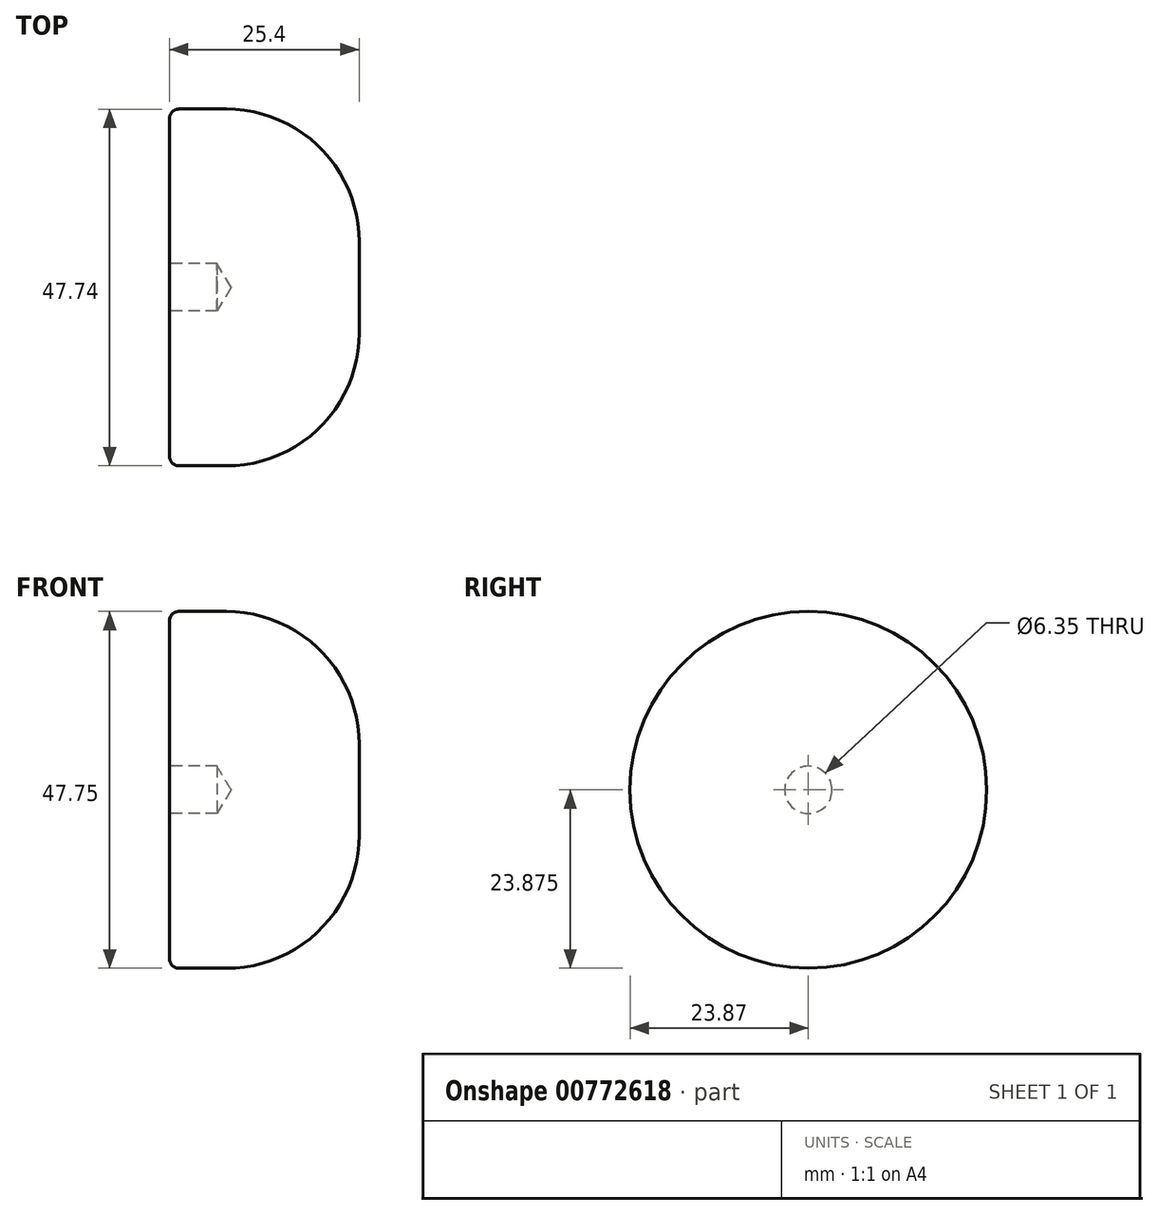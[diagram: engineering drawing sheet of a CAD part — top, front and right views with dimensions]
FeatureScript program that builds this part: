
annotation { "Feature Type Name" : "Feature", "Feature Type Description" : "" }
export const myFeature = defineFeature(function(context is Context, id is Id, definition is map)
    precondition{}
    {
        {
            var Q0;
            Q0=qCreatedBy(makeId("Right.planeOp"),FACE);
            var sketch = newSketch(context, id + "F0", { "sketchPlane" : qUnion([Q0])});
            skCircle(sketch, "E0", {"center": v(0, 17.6) * mm, "radius": 23.87 * mm});
            skSolve(sketch);
        }
        {
            var Q0;
            Q0 = qSketchRegion(id + "F0", true);
            extrude(context, id + "F1", {"entities" : qUnion([Q0]), "oppositeDirection" : true, "depth" : 25.4 * mm, "offsetDistance" : 25.4 * mm});
        }
        {
            var Q0;
            Q0=makeQuery(id+"F1.opExtrude","CAP_EDGE",EDGE,{"disambiguationData":[OSD([sQuery(id+"F0.wireOp",EDGE,"E0")])],"isStart":true});
            fillet(context, id + "F2", {"entities" : qUnion([Q0]), "radius" : 17.78 * mm, "tangentPropagation" : true, "allowEdgeOverflow" : false});
        }
        {
            var Q0;
            Q0=makeQuery(id+"F1.opExtrude","CAP_FACE",FACE,{"disambiguationData":[OSD([sQuery(id+"F0.wireOp",EDGE,"E0")])],"isStart":false});
            var sketch = newSketch(context, id + "F3", { "sketchPlane" : qUnion([Q0])});
            skCircle(sketch, "E1", {"center": v(0, 17.6) * mm, "radius": 6.9 * mm});
            skSolve(sketch);
        }
        {
            var Q0;
            Q0=sQuery(id+"F3.wireOp",VERTEX,"E1.center");
            var Q1;
            Q1=makeQuery(id+"F1.opExtrude","SWEPT_BODY",BODY,{"disambiguationData":[OSD([sQuery(id+"F0.wireOp",EDGE,"E0")])]});
            hole(context, id + "F4", {"style" : HoleStyle.SIMPLE, "endStyle" : HoleEndStyle.BLIND, "holeDiameter" : 6.35 * mm, "majorDiameter" : 6.35 * mm, "holeDepth" : 6.35 * mm, "isTappedThrough" : true, "tappedDepth" : 12.7 * mm, "tapClearance" : 3, "locations" : qUnion([Q0]), "scope" : qUnion([Q1])});
        }
        {
            var Q0;
            Q0=makeQuery(id+"F1.opExtrude","CAP_EDGE",EDGE,{"disambiguationData":[OSD([sQuery(id+"F0.wireOp",EDGE,"E0")])],"isStart":false});
            fillet(context, id + "F5", {"entities" : qUnion([Q0]), "radius" : 1.27 * mm, "tangentPropagation" : true, "allowEdgeOverflow" : false});
        }
    });
